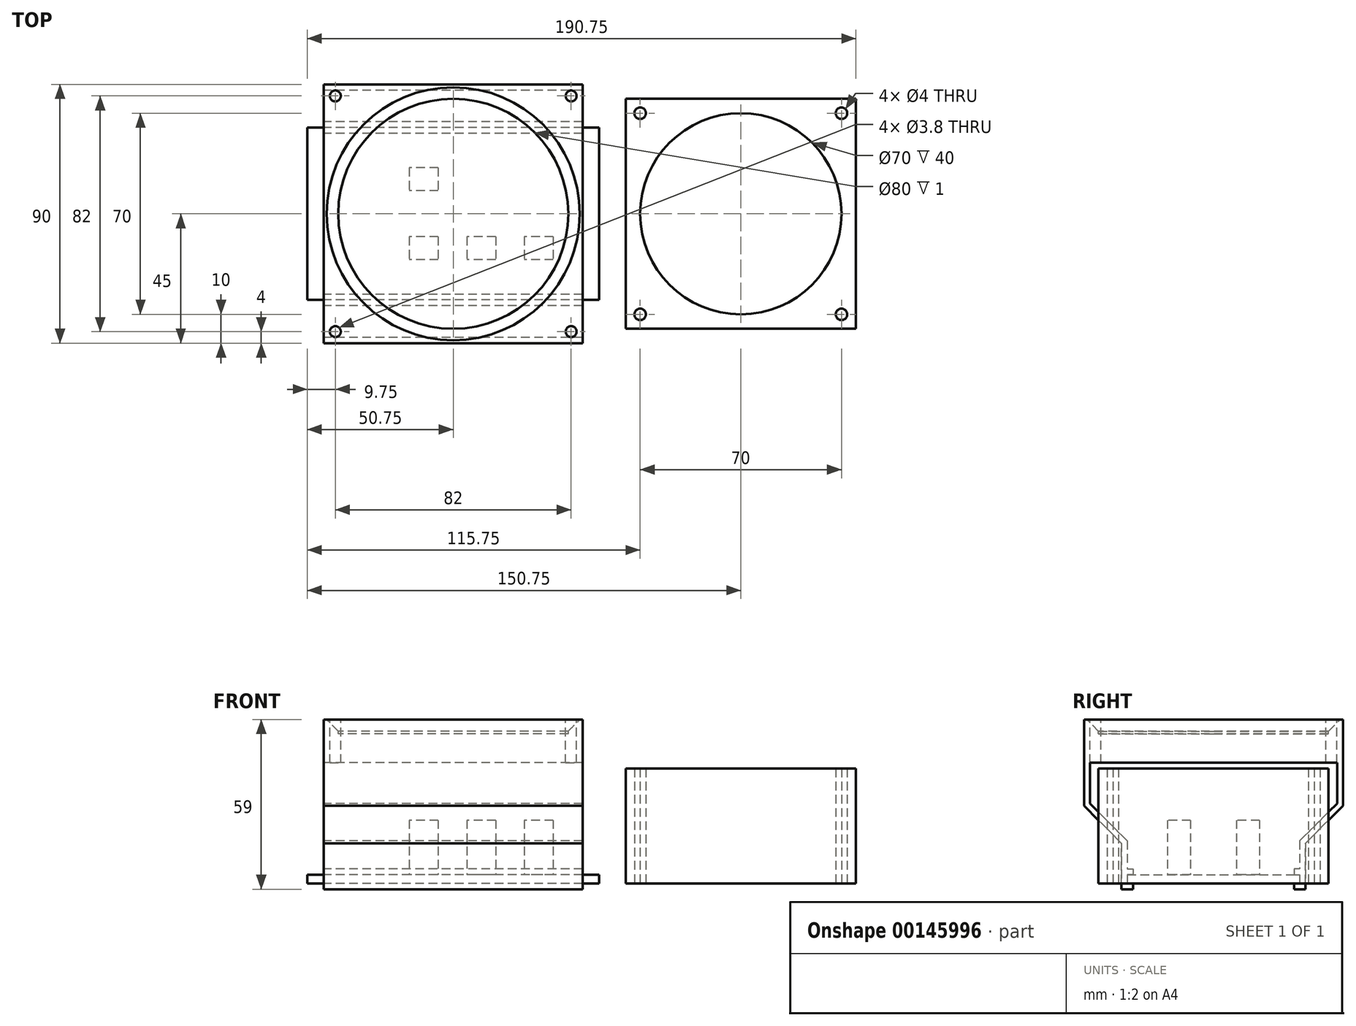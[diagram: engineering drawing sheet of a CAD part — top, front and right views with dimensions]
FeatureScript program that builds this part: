
annotation { "Feature Type Name" : "Feature", "Feature Type Description" : "" }
export const myFeature = defineFeature(function(context is Context, id is Id, definition is map)
    precondition{}
    {
        {
            var Q0;
            Q0=qCreatedBy(makeId("Top.planeOp"),FACE);
            var sketch = newSketch(context, id + "F0", { "sketchPlane" : qUnion([Q0])});
            skLineSegment(sketch, "E0.bottom", {"start": v(50.75, -30) * mm, "end": v(-50.75, -30) * mm});
            skLineSegment(sketch, "E0.top", {"start": v(50.75, 30) * mm, "end": v(-50.75, 30) * mm});
            skLineSegment(sketch, "E0.left", {"start": v(50.75, -30) * mm, "end": v(50.75, 30) * mm});
            skLineSegment(sketch, "E0.right", {"start": v(-50.75, -30) * mm, "end": v(-50.75, 30) * mm});
            skPoint(sketch, "E0.middle", {"position": v(0, 0) * mm});
            skSolve(sketch);
        }
        {
            var Q0;
            Q0 = qSketchRegion(id + "F0", true);
            extrude(context, id + "F1", {"entities" : qUnion([Q0]), "depth" : 3 * mm});
        }
        {
            var Q0;
            Q0=makeQuery(id+"F1.opExtrude","CAP_FACE",FACE,{"disambiguationData":[OSD([sQuery(id+"F0.wireOp",EDGE,"E0.bottom"),sQuery(id+"F0.wireOp",EDGE,"E0.top"),sQuery(id+"F0.wireOp",EDGE,"E0.left"),sQuery(id+"F0.wireOp",EDGE,"E0.right")])],"isStart":false});
            var sketch = newSketch(context, id + "F2", { "sketchPlane" : qUnion([Q0])});
            skLineSegment(sketch, "E1.bottom", {"start": v(34.75, -8) * mm, "end": v(24.75, -8) * mm});
            skLineSegment(sketch, "E1.top", {"start": v(34.75, -16) * mm, "end": v(24.75, -16) * mm});
            skLineSegment(sketch, "E1.left", {"start": v(34.75, -8) * mm, "end": v(34.75, -16) * mm});
            skLineSegment(sketch, "E1.right", {"start": v(24.75, -8) * mm, "end": v(24.75, -16) * mm});
            skLineSegment(sketch, "E2.bottom", {"start": v(50.75, -30) * mm, "end": v(34.75, -30) * mm, "construction": true});
            skLineSegment(sketch, "E2.top", {"start": v(50.75, -16) * mm, "end": v(34.75, -16) * mm, "construction": true});
            skLineSegment(sketch, "E2.left", {"start": v(50.75, -30) * mm, "end": v(50.75, -16) * mm, "construction": true});
            skLineSegment(sketch, "E2.right", {"start": v(34.75, -30) * mm, "end": v(34.75, -16) * mm, "construction": true});
            skLineSegment(sketch, "E3", {"start": v(34.75, -16) * mm, "end": v(14.75, -16) * mm, "construction": true});
            skLineSegment(sketch, "E4", {"start": v(14.75, -16) * mm, "end": v(-5.25, -16) * mm, "construction": true});
            skLineSegment(sketch, "E5.bottom", {"start": v(14.75, -8) * mm, "end": v(4.75, -8) * mm});
            skLineSegment(sketch, "E5.top", {"start": v(14.75, -16) * mm, "end": v(4.75, -16) * mm});
            skLineSegment(sketch, "E5.left", {"start": v(14.75, -8) * mm, "end": v(14.75, -16) * mm});
            skLineSegment(sketch, "E5.right", {"start": v(4.75, -8) * mm, "end": v(4.75, -16) * mm});
            skLineSegment(sketch, "E6.bottom", {"start": v(-5.25, -8) * mm, "end": v(-15.25, -8) * mm});
            skLineSegment(sketch, "E6.top", {"start": v(-5.25, -16) * mm, "end": v(-15.25, -16) * mm});
            skLineSegment(sketch, "E6.left", {"start": v(-5.25, -8) * mm, "end": v(-5.25, -16) * mm});
            skLineSegment(sketch, "E6.right", {"start": v(-15.25, -8) * mm, "end": v(-15.25, -16) * mm});
            skLineSegment(sketch, "E7", {"start": v(-5.25, -30) * mm, "end": v(-5.25, 8) * mm, "construction": true});
            skLineSegment(sketch, "E8.bottom", {"start": v(-5.25, 16) * mm, "end": v(-15.25, 16) * mm});
            skLineSegment(sketch, "E8.top", {"start": v(-5.25, 8) * mm, "end": v(-15.25, 8) * mm});
            skLineSegment(sketch, "E8.left", {"start": v(-5.25, 16) * mm, "end": v(-5.25, 8) * mm});
            skLineSegment(sketch, "E8.right", {"start": v(-15.25, 16) * mm, "end": v(-15.25, 8) * mm});
            skSolve(sketch);
        }
        {
            var Q0;
            Q0 = qSketchRegion(id + "F2", true);
            extrude(context, id + "F3", {"entities" : qUnion([Q0]), "operationType" : NewBodyOperationType.ADD, "depth" : 19 * mm});
        }
        {
            var Q0;
            Q0=qCreatedBy(makeId("Top.planeOp"),FACE);
            var sketch = newSketch(context, id + "F4", { "sketchPlane" : qUnion([Q0])});
            skLineSegment(sketch, "E9.bottom", {"start": v(140, 40) * mm, "end": v(60, 40) * mm});
            skLineSegment(sketch, "E9.top", {"start": v(140, -40) * mm, "end": v(60, -40) * mm});
            skLineSegment(sketch, "E9.left", {"start": v(140, 40) * mm, "end": v(140, -40) * mm});
            skLineSegment(sketch, "E9.right", {"start": v(60, 40) * mm, "end": v(60, -40) * mm});
            skPoint(sketch, "E9.middle", {"position": v(100, 0) * mm});
            skLineSegment(sketch, "E10.bottom", {"start": v(135, 35) * mm, "end": v(65, 35) * mm, "construction": true});
            skLineSegment(sketch, "E10.top", {"start": v(135, -35) * mm, "end": v(65, -35) * mm, "construction": true});
            skLineSegment(sketch, "E10.left", {"start": v(135, 35) * mm, "end": v(135, -35) * mm, "construction": true});
            skLineSegment(sketch, "E10.right", {"start": v(65, 35) * mm, "end": v(65, -35) * mm, "construction": true});
            skLineSegment(sketch, "E11", {"start": v(100, 0) * mm, "end": v(0, 0) * mm, "construction": true});
            skSolve(sketch);
        }
        {
            var Q0;
            Q0 = qSketchRegion(id + "F4", true);
            extrude(context, id + "F5", {"entities" : qUnion([Q0]), "depth" : 40 * mm});
        }
        {
            var Q0;
            Q0=sQuery(id+"F4.wireOp",VERTEX,"E9.middle");
            var Q1;
            Q1=makeQuery(id+"F5.opExtrude","SWEPT_BODY",BODY,{"disambiguationData":[OSD([sQuery(id+"F4.wireOp",EDGE,"E9.bottom"),sQuery(id+"F4.wireOp",EDGE,"E9.top"),sQuery(id+"F4.wireOp",EDGE,"E9.left"),sQuery(id+"F4.wireOp",EDGE,"E9.right")])]});
            hole(context, id + "F6", {"style" : HoleStyle.SIMPLE, "endStyle" : HoleEndStyle.THROUGH, "oppositeDirection" : true, "holeDiameter" : 70 * mm, "locations" : qUnion([Q0]), "scope" : qUnion([Q1]), "isTappedThrough" : true});
        }
        {
            var Q0;
            Q0=sQuery(id+"F4.wireOp",VERTEX,"E10.left.start");
            var Q1;
            Q1=sQuery(id+"F4.wireOp",VERTEX,"E10.bottom.end");
            var Q2;
            Q2=sQuery(id+"F4.wireOp",VERTEX,"E10.top.end");
            var Q3;
            Q3=sQuery(id+"F4.wireOp",VERTEX,"E10.top.start");
            var Q4;
            Q4=makeQuery(id+"F5.opExtrude","SWEPT_BODY",BODY,{"disambiguationData":[OSD([sQuery(id+"F4.wireOp",EDGE,"E9.bottom"),sQuery(id+"F4.wireOp",EDGE,"E9.top"),sQuery(id+"F4.wireOp",EDGE,"E9.left"),sQuery(id+"F4.wireOp",EDGE,"E9.right")])]});
            hole(context, id + "F7", {"style" : HoleStyle.SIMPLE, "endStyle" : HoleEndStyle.THROUGH, "oppositeDirection" : true, "holeDiameter" : 4 * mm, "locations" : qUnion([Q0, Q1, Q2, Q3]), "scope" : qUnion([Q4]), "isTappedThrough" : true});
        }
        {
            var Q0;
            Q0=makeQuery(id+"F3.opExtrude","CAP_FACE",FACE,{"disambiguationData":[OSD([sQuery(id+"F2.wireOp",EDGE,"E6.bottom"),sQuery(id+"F2.wireOp",EDGE,"E6.top"),sQuery(id+"F2.wireOp",EDGE,"E6.left"),sQuery(id+"F2.wireOp",EDGE,"E6.right")])],"isStart":false});
            cPlane(context, id + "F8", {"entities" : qUnion([Q0]), "cplaneType" : CPlaneType.OFFSET, "offset" : 35 * mm, "width" : 150 * mm, "height" : 150 * mm});
        }
        {
            var Q0;
            Q0=qCreatedBy(id+"F8.planeOp",FACE);
            var sketch = newSketch(context, id + "F9", { "sketchPlane" : qUnion([Q0])});
            skLineSegment(sketch, "E12.bottom", {"start": v(45, 45) * mm, "end": v(-45, 45) * mm});
            skLineSegment(sketch, "E12.top", {"start": v(45, -45) * mm, "end": v(-45, -45) * mm});
            skLineSegment(sketch, "E12.left", {"start": v(45, 45) * mm, "end": v(45, -45) * mm});
            skLineSegment(sketch, "E12.right", {"start": v(-45, 45) * mm, "end": v(-45, -45) * mm});
            skPoint(sketch, "E12.middle", {"position": v(0, 0) * mm});
            skLineSegment(sketch, "E13.bottom", {"start": v(-41, 41) * mm, "end": v(41, 41) * mm, "construction": true});
            skLineSegment(sketch, "E13.top", {"start": v(-41, -41) * mm, "end": v(41, -41) * mm, "construction": true});
            skLineSegment(sketch, "E13.left", {"start": v(-41, 41) * mm, "end": v(-41, -41) * mm, "construction": true});
            skLineSegment(sketch, "E13.right", {"start": v(41, 41) * mm, "end": v(41, -41) * mm, "construction": true});
            skCircle(sketch, "E14", {"center": v(0, 0) * mm, "radius": 40 * mm});
            skSolve(sketch);
        }
        {
            var Q0;
            Q0 = qSketchRegion(id + "F9", true);
            extrude(context, id + "F10", {"entities" : qUnion([Q0]), "oppositeDirection" : true, "depth" : 5 * mm});
        }
        {
            var Q0;
            Q0=makeQuery(id+"F10.opExtrude","CAP_FACE",FACE,{"disambiguationData":[OSD([sQuery(id+"F9.wireOp",EDGE,"E12.bottom"),sQuery(id+"F9.wireOp",EDGE,"E12.top"),sQuery(id+"F9.wireOp",EDGE,"E12.left"),sQuery(id+"F9.wireOp",EDGE,"E12.right")])],"isStart":false});
            var sketch = newSketch(context, id + "F11", { "sketchPlane" : qUnion([Q0])});
            skLineSegment(sketch, "E15.bottom", {"start": v(-45, -45) * mm, "end": v(45, -45) * mm});
            skLineSegment(sketch, "E15.top", {"start": v(-45, 45) * mm, "end": v(45, 45) * mm});
            skLineSegment(sketch, "E15.left", {"start": v(-45, -45) * mm, "end": v(-45, 45) * mm});
            skLineSegment(sketch, "E15.right", {"start": v(45, -45) * mm, "end": v(45, 45) * mm});
            skSolve(sketch);
        }
        {
            var Q0;
            Q0=makeQuery(id+"F11.imprint","IMPRINT",FACE,{"disambiguationData":[TD([[makeQuery(id+"F11.imprint","IMPRINT",EDGE,{"derivedFrom":sQuery(id+"F11.wireOp",EDGE,"E15.bottom")}),-1.0]])]});
            var sketch = newSketch(context, id + "F12", { "sketchPlane" : qUnion([Q0])});
            skLineSegment(sketch, "E16.bottom", {"start": v(-45, 45) * mm, "end": v(45, 45) * mm});
            skLineSegment(sketch, "E16.top", {"start": v(-45, -45) * mm, "end": v(45, -45) * mm});
            skLineSegment(sketch, "E16.left", {"start": v(-45, 45) * mm, "end": v(-45, -45) * mm});
            skLineSegment(sketch, "E16.right", {"start": v(45, 45) * mm, "end": v(45, -45) * mm});
            skSolve(sketch);
        }
        {
            var Q0;
            Q0 = qSketchRegion(id + "F12", true);
            extrude(context, id + "F13", {"entities" : qUnion([Q0]), "operationType" : NewBodyOperationType.ADD, "depth" : 10 * mm});
        }
        {
            var Q0;
            Q0=makeQuery(id+"F13.opExtrude","CAP_FACE",FACE,{"disambiguationData":[OSD([sQuery(id+"F12.wireOp",EDGE,"E16.bottom"),sQuery(id+"F12.wireOp",EDGE,"E16.top"),sQuery(id+"F12.wireOp",EDGE,"E16.left"),sQuery(id+"F12.wireOp",EDGE,"E16.right")])],"isStart":false});
            cPlane(context, id + "F14", {"entities" : qUnion([Q0]), "cplaneType" : CPlaneType.OFFSET, "offset" : 0 * mm, "width" : 150 * mm, "height" : 150 * mm});
        }
        {
            var Q0;
            Q0=makeQuery(id+"F10.opExtrude","CAP_EDGE",EDGE,{"disambiguationData":[OSD([sQuery(id+"F9.wireOp",EDGE,"E14")])],"isStart":true});
            chamfer(context, id + "F15", {"entities" : qUnion([Q0]), "width" : 4 * mm, "tangentPropagation" : true});
        }
        {
            var Q0;
            Q0=sQuery(id+"F9.wireOp",VERTEX,"E13.left.start");
            var Q1;
            Q1=sQuery(id+"F9.wireOp",VERTEX,"E13.right.start");
            var Q2;
            Q2=sQuery(id+"F9.wireOp",VERTEX,"E13.right.end");
            var Q3;
            Q3=sQuery(id+"F9.wireOp",VERTEX,"E13.left.end");
            var Q4;
            Q4=makeQuery(id+"F10.opExtrude","SWEPT_BODY",BODY,{"disambiguationData":[OSD([sQuery(id+"F9.wireOp",EDGE,"E12.bottom"),sQuery(id+"F9.wireOp",EDGE,"E12.top"),sQuery(id+"F9.wireOp",EDGE,"E12.left"),sQuery(id+"F9.wireOp",EDGE,"E12.right"),sQuery(id+"F9.wireOp",EDGE,"E14")])]});
            hole(context, id + "F16", {"style" : HoleStyle.SIMPLE, "endStyle" : HoleEndStyle.THROUGH, "holeDiameter" : 3.8 * mm, "locations" : qUnion([Q0, Q1, Q2, Q3]), "scope" : qUnion([Q4]), "isTappedThrough" : true});
        }
        {
            var Q0;
            Q0=makeQuery(id+"F10.opExtrude","SWEPT_FACE",FACE,{"disambiguationData":[OSD([sQuery(id+"F9.wireOp",EDGE,"E12.right")])]});
            var sketch = newSketch(context, id + "F17", { "sketchPlane" : qUnion([Q0])});
            skLineSegment(sketch, "E17", {"start": v(43, 42) * mm, "end": v(45, 42) * mm});
            skLineSegment(sketch, "E18", {"start": v(45, 42) * mm, "end": v(45, 27) * mm});
            skLineSegment(sketch, "E19", {"start": v(45, 27) * mm, "end": v(32, 14) * mm});
            skLineSegment(sketch, "E20", {"start": v(32, 14) * mm, "end": v(32, -2) * mm});
            skLineSegment(sketch, "E21", {"start": v(32, -2) * mm, "end": v(28, -2) * mm});
            skLineSegment(sketch, "E22", {"start": v(28, -2) * mm, "end": v(28, 0) * mm});
            skLineSegment(sketch, "E23", {"start": v(28, 0) * mm, "end": v(30, 0) * mm});
            skLineSegment(sketch, "E24", {"start": v(30, 14.83) * mm, "end": v(43, 27.83) * mm});
            skLineSegment(sketch, "E25", {"start": v(43, 27.83) * mm, "end": v(43, 42) * mm});
            skLineSegment(sketch, "E26", {"start": v(30, 0) * mm, "end": v(30, 3) * mm});
            skLineSegment(sketch, "E27", {"start": v(30, 3) * mm, "end": v(28, 3) * mm});
            skLineSegment(sketch, "E28", {"start": v(28, 3) * mm, "end": v(28, 5) * mm});
            skLineSegment(sketch, "E29", {"start": v(28, 5) * mm, "end": v(30, 5) * mm});
            skLineSegment(sketch, "E30", {"start": v(30, 5) * mm, "end": v(30, 14.83) * mm});
            skLineSegment(sketch, "E31", {"start": v(0, 57) * mm, "end": v(0, 26.43) * mm, "construction": true});
            skLineSegment(sketch, "E32.MirrorCS", {"start": v(-30, 3) * mm, "end": v(-28, 3) * mm});
            skLineSegment(sketch, "E33.MirrorCS", {"start": v(-28, 3) * mm, "end": v(-28, 5) * mm});
            skLineSegment(sketch, "E34.MirrorCS", {"start": v(-28, 0) * mm, "end": v(-30, 0) * mm});
            skLineSegment(sketch, "E35.MirrorCS", {"start": v(-30, 0) * mm, "end": v(-30, 3) * mm});
            skLineSegment(sketch, "E36.MirrorCS", {"start": v(-28, -2) * mm, "end": v(-28, 0) * mm});
            skLineSegment(sketch, "E37.MirrorCS", {"start": v(-30, 5) * mm, "end": v(-30, 14.83) * mm});
            skLineSegment(sketch, "E38.MirrorCS", {"start": v(-28, 5) * mm, "end": v(-30, 5) * mm});
            skLineSegment(sketch, "E39.MirrorCS", {"start": v(-32, -2) * mm, "end": v(-28, -2) * mm});
            skLineSegment(sketch, "E40.MirrorCS", {"start": v(-43, 42) * mm, "end": v(-45, 42) * mm});
            skLineSegment(sketch, "E41.MirrorCS", {"start": v(-43, 27.83) * mm, "end": v(-43, 42) * mm});
            skLineSegment(sketch, "E42.MirrorCS", {"start": v(-30, 14.83) * mm, "end": v(-43, 27.83) * mm});
            skLineSegment(sketch, "E43.MirrorCS", {"start": v(-45, 27) * mm, "end": v(-32, 14) * mm});
            skLineSegment(sketch, "E44.MirrorCS", {"start": v(-45, 42) * mm, "end": v(-45, 27) * mm});
            skLineSegment(sketch, "E45.MirrorCS", {"start": v(-32, 14) * mm, "end": v(-32, -2) * mm});
            skSolve(sketch);
        }
        {
            var Q0;
            Q0=makeQuery(id+"F17.imprint","IMPRINT",FACE,{"disambiguationData":[TD([[makeQuery(id+"F17.imprint","IMPRINT",EDGE,{"derivedFrom":sQuery(id+"F17.wireOp",EDGE,"E17")}),-1.0]])]});
            var Q1;
            Q1=makeQuery(id+"F17.imprint","IMPRINT",FACE,{"disambiguationData":[TD([[makeQuery(id+"F17.imprint","IMPRINT",EDGE,{"derivedFrom":sQuery(id+"F17.wireOp",EDGE,"E32.MirrorCS")}),1.0]])]});
            var Q2;
            Q2=makeQuery(id+"F10.opExtrude","SWEPT_FACE",FACE,{"disambiguationData":[OSD([sQuery(id+"F9.wireOp",EDGE,"E12.left")])]});
            extrude(context, id + "F18", {"entities" : qUnion([Q0, Q1]), "operationType" : NewBodyOperationType.ADD, "endBound" : BoundingType.UP_TO_SURFACE, "oppositeDirection" : true, "endBoundEntityFace" : qUnion([Q2]), "depth" : 25 * mm});
        }
    });
